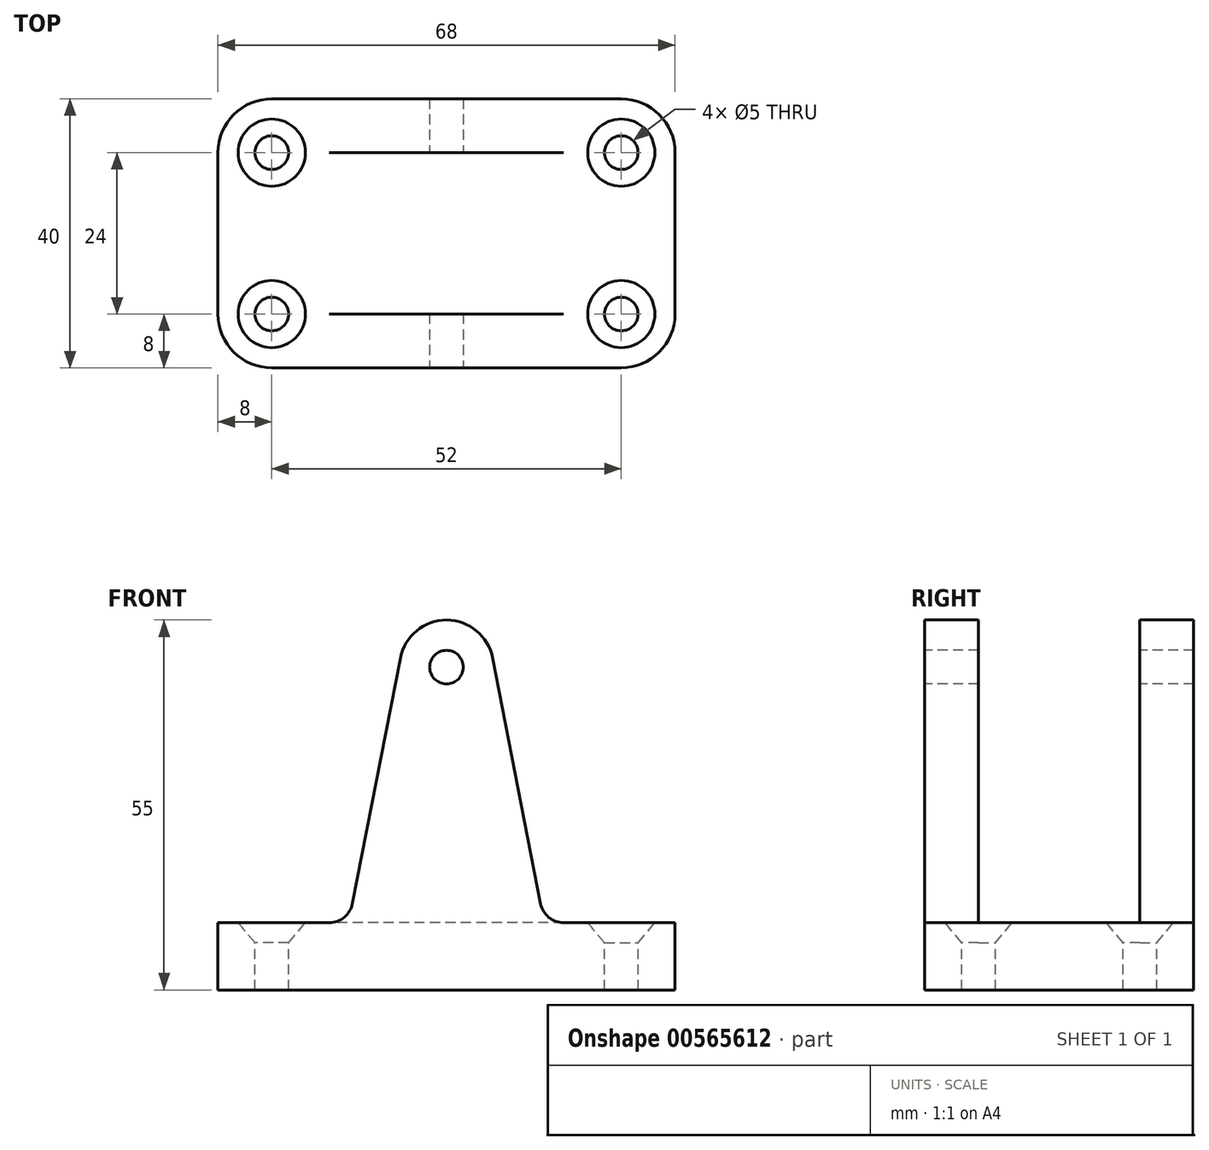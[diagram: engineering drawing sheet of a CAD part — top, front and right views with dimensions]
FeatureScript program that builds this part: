
annotation { "Feature Type Name" : "Feature", "Feature Type Description" : "" }
export const myFeature = defineFeature(function(context is Context, id is Id, definition is map)
    precondition{}
    {
        {
            var Q0;
            Q0=qCreatedBy(makeId("Top.planeOp"),FACE);
            var sketch = newSketch(context, id + "F0", { "sketchPlane" : qUnion([Q0])});
            skPoint(sketch, "E0.middle", {"position": v(0, 0) * mm});
            skLineSegment(sketch, "E1.bottom", {"start": v(26, 20) * mm, "end": v(-26, 20) * mm});
            skLineSegment(sketch, "E1.top", {"start": v(26, -20) * mm, "end": v(-26, -20) * mm});
            skLineSegment(sketch, "E1.left", {"start": v(34, 12) * mm, "end": v(34, -12) * mm});
            skLineSegment(sketch, "E1.right", {"start": v(-34, 12) * mm, "end": v(-34, -12) * mm});
            skPoint(sketch, "E2.visualSharp", {"position": v(-34, -20) * mm});
            skArc(sketch, "E2.filletArc", {"start": v(-34, -12) * mm, "mid": v(-31.66, -17.66) * mm, "end": v(-26, -20) * mm});
            skPoint(sketch, "E3.visualSharp", {"position": v(-34, 20) * mm});
            skArc(sketch, "E3.filletArc", {"start": v(-26, 20) * mm, "mid": v(-31.66, 17.66) * mm, "end": v(-34, 12) * mm});
            skPoint(sketch, "E4.visualSharp", {"position": v(34, 20) * mm});
            skArc(sketch, "E4.filletArc", {"start": v(34, 12) * mm, "mid": v(31.66, 17.66) * mm, "end": v(26, 20) * mm});
            skPoint(sketch, "E5.visualSharp", {"position": v(34, -20) * mm});
            skArc(sketch, "E5.filletArc", {"start": v(26, -20) * mm, "mid": v(31.66, -17.66) * mm, "end": v(34, -12) * mm});
            skSolve(sketch);
        }
        {
            var Q0;
            Q0=qSketchRegion(id+"F0",true);
            extrude(context, id + "F1", {"entities" : qUnion([Q0]), "oppositeDirection" : true, "depth" : 10 * mm});
        }
        {
            var Q0;
            Q0=makeQuery(id+"F1.opExtrude","CAP_FACE",FACE,{"disambiguationData":[OSD([sQuery(id+"F0.wireOp",EDGE,"E1.bottom"),sQuery(id+"F0.wireOp",EDGE,"E1.top"),sQuery(id+"F0.wireOp",EDGE,"E1.left"),sQuery(id+"F0.wireOp",EDGE,"E1.right"),sQuery(id+"F0.wireOp",EDGE,"E2.filletArc"),sQuery(id+"F0.wireOp",EDGE,"E3.filletArc"),sQuery(id+"F0.wireOp",EDGE,"E4.filletArc"),sQuery(id+"F0.wireOp",EDGE,"E5.filletArc")])],"isStart":true});
            var sketch = newSketch(context, id + "F2", { "sketchPlane" : qUnion([Q0])});
            skCircle(sketch, "E6", {"center": v(-26, 12) * mm, "radius": 2.5 * mm});
            skCircle(sketch, "E7", {"center": v(26, 12) * mm, "radius": 2.5 * mm});
            skCircle(sketch, "E8", {"center": v(26, -12) * mm, "radius": 2.5 * mm});
            skCircle(sketch, "E9", {"center": v(-26, -12) * mm, "radius": 2.5 * mm});
            skSolve(sketch);
        }
        {
            var Q0;
            Q0=makeQuery(id+"F2.imprint","IMPRINT",FACE,{"disambiguationData":[TD([[makeQuery(id+"F2.imprint","IMPRINT",EDGE,{"derivedFrom":sQuery(id+"F2.wireOp",EDGE,"E6")}),1.0]])]});
            var Q1;
            Q1=makeQuery(id+"F2.imprint","IMPRINT",FACE,{"disambiguationData":[TD([[makeQuery(id+"F2.imprint","IMPRINT",EDGE,{"derivedFrom":sQuery(id+"F2.wireOp",EDGE,"E9")}),1.0]])]});
            var Q2;
            Q2=makeQuery(id+"F2.imprint","IMPRINT",FACE,{"disambiguationData":[TD([[makeQuery(id+"F2.imprint","IMPRINT",EDGE,{"derivedFrom":sQuery(id+"F2.wireOp",EDGE,"E8")}),1.0]])]});
            var Q3;
            Q3=makeQuery(id+"F2.imprint","IMPRINT",FACE,{"disambiguationData":[TD([[makeQuery(id+"F2.imprint","IMPRINT",EDGE,{"derivedFrom":sQuery(id+"F2.wireOp",EDGE,"E7")}),1.0]])]});
            extrude(context, id + "F3", {"entities" : qUnion([Q0, Q1, Q2, Q3]), "operationType" : NewBodyOperationType.REMOVE, "oppositeDirection" : true, "depth" : 25 * mm});
        }
        {
            var Q0;
            Q0=makeQuery(id+"F1.opExtrude","SWEPT_FACE",FACE,{"disambiguationData":[OSD([sQuery(id+"F0.wireOp",EDGE,"E1.top")])]});
            var sketch = newSketch(context, id + "F4", { "sketchPlane" : qUnion([Q0])});
            skCircle(sketch, "E10", {"center": v(0, 38) * mm, "radius": 2.5 * mm});
            skCircle(sketch, "E11", {"center": v(0, 38) * mm, "radius": 7 * mm});
            skLineSegment(sketch, "E12", {"start": v(-14, 2.83) * mm, "end": v(-6.87, 39.34) * mm});
            skArc(sketch, "E13.filletArc", {"start": v(-17.44, 0) * mm, "mid": v(-15.21, 0.8) * mm, "end": v(-14, 2.83) * mm});
            skLineSegment(sketch, "E14", {"start": v(0, 0) * mm, "end": v(-20.16, 0) * mm});
            skLineSegment(sketch, "E15.MirrorCS", {"start": v(14, 2.83) * mm, "end": v(6.87, 39.34) * mm});
            skArc(sketch, "E16.MirrorCS", {"start": v(17.44, 0) * mm, "mid": v(15.21, 0.8) * mm, "end": v(14, 2.83) * mm});
            skLineSegment(sketch, "E17.MirrorCS", {"start": v(0, 0) * mm, "end": v(20.16, 0) * mm});
            skSolve(sketch);
        }
        {
            var Q0;
            {var subQ4=sQuery(id+"F4.wireOp",EDGE,"E12");Q0=makeQuery(id+"F4.imprint","IMPRINT",FACE,{"disambiguationData":[TD([[makeQuery(id+"F4.imprint","IMPRINT",EDGE,{"derivedFrom":subQ4}),-1.0]])]});}
            var Q1;
            Q1=makeQuery(id+"F4.imprint","IMPRINT",FACE,{"disambiguationData":[TD([[makeQuery(id+"F4.imprint","IMPRINT",EDGE,{"derivedFrom":sQuery(id+"F4.wireOp",EDGE,"E10")}),-1.0]])]});
            extrude(context, id + "F5", {"entities" : qUnion([Q0, Q1]), "operationType" : NewBodyOperationType.ADD, "oppositeDirection" : true, "depth" : 8 * mm});
        }
        {
            var Q0;
            Q0=qSketchRegion(id+"F4",true);
            extrude(context, id + "F6", {"entities" : qUnion([Q0]), "operationType" : NewBodyOperationType.ADD, "oppositeDirection" : true, "depth" : 40 * mm, "hasSecondDirection" : true, "secondDirectionOppositeDirection" : true, "secondDirectionDepth" : 32 * mm});
        }
        {
            var Q0;
            Q0=makeQuery(id+"F5.boolean.opBoolean","MERGE",FACE,{"derivedFrom":[makeQuery(id+"F1.opExtrude","SWEPT_FACE",FACE,{"disambiguationData":[OSD([sQuery(id+"F0.wireOp",EDGE,"E1.top")])]}),makeQuery(id+"F5.opExtrude","CAP_FACE",FACE,{"disambiguationData":[OSD([sQuery(id+"F4.wireOp",EDGE,"E10"),sQuery(id+"F4.wireOp",EDGE,"E11"),sQuery(id+"F4.wireOp",EDGE,"E12"),sQuery(id+"F4.wireOp",EDGE,"E13.filletArc"),sQuery(id+"F4.wireOp",EDGE,"E14"),sQuery(id+"F4.wireOp",EDGE,"E15.MirrorCS"),sQuery(id+"F4.wireOp",EDGE,"E16.MirrorCS"),sQuery(id+"F4.wireOp",EDGE,"E17.MirrorCS")])],"isStart":true})]});
            cPlane(context, id + "F7", {"entities" : qUnion([Q0]), "cplaneType" : CPlaneType.OFFSET, "offset" : 8 * mm, "oppositeDirection" : true, "width" : 150 * mm, "height" : 150 * mm});
        }
        {
            var Q0;
            Q0=qCreatedBy(id+"F7.planeOp",FACE);
            var sketch = newSketch(context, id + "F8", { "sketchPlane" : qUnion([Q0])});
            skLineSegment(sketch, "E18", {"start": v(-26, 0) * mm, "end": v(-26, -3) * mm});
            skLineSegment(sketch, "E19", {"start": v(-26, -3) * mm, "end": v(-23.5, -3) * mm});
            skLineSegment(sketch, "E20", {"start": v(-26, 0) * mm, "end": v(-21, 0) * mm});
            skLineSegment(sketch, "E21", {"start": v(-21, 0) * mm, "end": v(-23.5, -3) * mm});
            skSolve(sketch);
        }
        {
            var Q0;
            Q0=qSketchRegion(id+"F8",true);
            var Q1;
            Q1=sQuery(id+"F8.wireOp",EDGE,"E18");
            revolve(context, id + "F9", {"operationType" : NewBodyOperationType.REMOVE, "entities" : qUnion([Q0]), "axis" : qUnion([Q1]), "revolveType" : RevolveType.FULL, "oppositeDirection" : true});
        }
        {
            var Q0;
            Q0=qCreatedBy(id+"F7.planeOp",FACE);
            var sketch = newSketch(context, id + "F10", { "sketchPlane" : qUnion([Q0])});
            skLineSegment(sketch, "E22", {"start": v(26, 0) * mm, "end": v(26, -3) * mm});
            skLineSegment(sketch, "E23", {"start": v(26, -3) * mm, "end": v(28.5, -3) * mm});
            skLineSegment(sketch, "E24", {"start": v(28.5, -3) * mm, "end": v(31, 0) * mm});
            skLineSegment(sketch, "E25", {"start": v(31, 0) * mm, "end": v(26, 0) * mm});
            skSolve(sketch);
        }
        {
            var Q0;
            Q0=qSketchRegion(id+"F10",true);
            var Q1;
            Q1=sQuery(id+"F10.wireOp",EDGE,"E22");
            revolve(context, id + "F11", {"operationType" : NewBodyOperationType.REMOVE, "entities" : qUnion([Q0]), "axis" : qUnion([Q1]), "revolveType" : RevolveType.FULL, "oppositeDirection" : true});
        }
        {
            var Q0;
            Q0=makeQuery(id+"F6.boolean.opBoolean","MERGE",FACE,{"derivedFrom":[makeQuery(id+"F1.opExtrude","SWEPT_FACE",FACE,{"disambiguationData":[OSD([sQuery(id+"F0.wireOp",EDGE,"E1.bottom")])]}),makeQuery(id+"F6.opExtrude","CAP_FACE",FACE,{"disambiguationData":[OSD([sQuery(id+"F4.wireOp",EDGE,"E10"),sQuery(id+"F4.wireOp",EDGE,"E11"),sQuery(id+"F4.wireOp",EDGE,"E12"),sQuery(id+"F4.wireOp",EDGE,"E13.filletArc"),sQuery(id+"F4.wireOp",EDGE,"E14"),sQuery(id+"F4.wireOp",EDGE,"E15.MirrorCS"),sQuery(id+"F4.wireOp",EDGE,"E16.MirrorCS"),sQuery(id+"F4.wireOp",EDGE,"E17.MirrorCS")])],"isStart":false})]});
            cPlane(context, id + "F12", {"entities" : qUnion([Q0]), "cplaneType" : CPlaneType.OFFSET, "offset" : 8 * mm, "oppositeDirection" : true, "width" : 150 * mm, "height" : 150 * mm});
        }
        {
            var Q0;
            Q0=qCreatedBy(id+"F12.planeOp",FACE);
            var sketch = newSketch(context, id + "F13", { "sketchPlane" : qUnion([Q0])});
            skLineSegment(sketch, "E26", {"start": v(-26, 0) * mm, "end": v(-31, 0) * mm});
            skLineSegment(sketch, "E27", {"start": v(-26, 0) * mm, "end": v(-26, -3) * mm});
            skLineSegment(sketch, "E28", {"start": v(-26, -3) * mm, "end": v(-28.5, -3) * mm});
            skLineSegment(sketch, "E29", {"start": v(-28.5, -3) * mm, "end": v(-31, 0) * mm});
            skSolve(sketch);
        }
        {
            var Q0;
            Q0=qSketchRegion(id+"F13",true);
            var Q1;
            Q1=sQuery(id+"F13.wireOp",EDGE,"E27");
            revolve(context, id + "F14", {"operationType" : NewBodyOperationType.REMOVE, "entities" : qUnion([Q0]), "axis" : qUnion([Q1]), "revolveType" : RevolveType.FULL, "oppositeDirection" : true});
        }
        {
            var Q0;
            Q0=qCreatedBy(id+"F12.planeOp",FACE);
            var sketch = newSketch(context, id + "F15", { "sketchPlane" : qUnion([Q0])});
            skLineSegment(sketch, "E30", {"start": v(26, 0) * mm, "end": v(26, -3) * mm});
            skLineSegment(sketch, "E31", {"start": v(26, -3) * mm, "end": v(28.5, -3) * mm});
            skLineSegment(sketch, "E32", {"start": v(28.5, -3) * mm, "end": v(31, 0) * mm});
            skLineSegment(sketch, "E33", {"start": v(31, 0) * mm, "end": v(26, 0) * mm});
            skSolve(sketch);
        }
        {
            var Q0;
            Q0=qSketchRegion(id+"F15",true);
            var Q1;
            Q1=sQuery(id+"F15.wireOp",EDGE,"E30");
            revolve(context, id + "F16", {"operationType" : NewBodyOperationType.REMOVE, "entities" : qUnion([Q0]), "axis" : qUnion([Q1]), "revolveType" : RevolveType.FULL, "oppositeDirection" : true});
        }
    });
